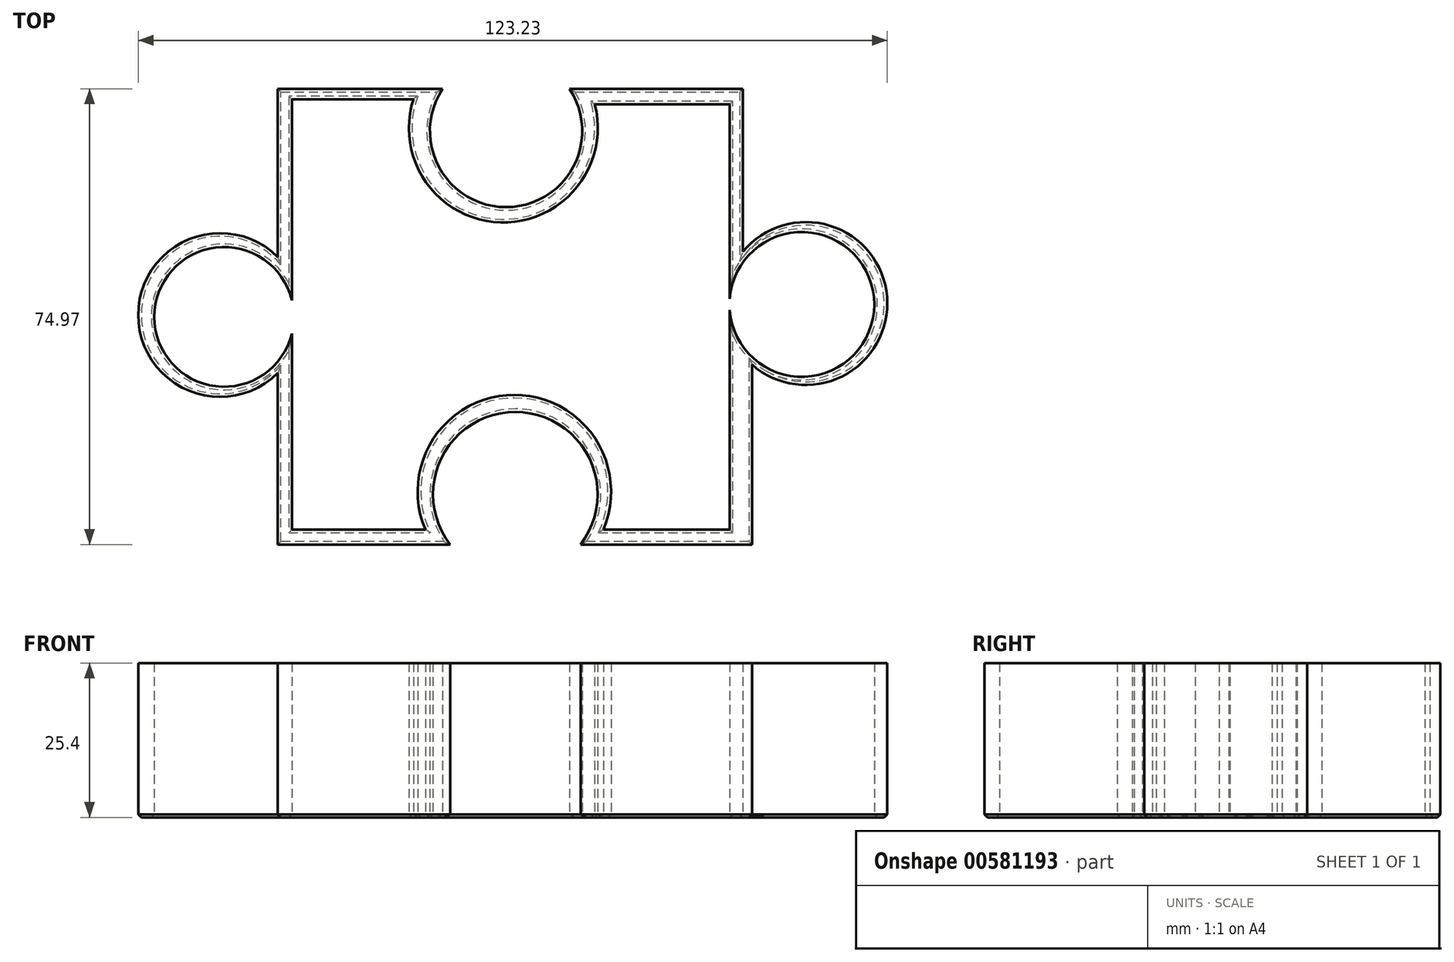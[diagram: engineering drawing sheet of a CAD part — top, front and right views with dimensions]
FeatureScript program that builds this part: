
annotation { "Feature Type Name" : "Feature", "Feature Type Description" : "" }
export const myFeature = defineFeature(function(context is Context, id is Id, definition is map)
    precondition{}
    {
        {
            var Q0;
            Q0=qCreatedBy(makeId("Top.planeOp"),FACE);
            var sketch = newSketch(context, id + "F0", { "sketchPlane" : qUnion([Q0])});
            skLineSegment(sketch, "E0", {"start": v(-36.92, 40.28) * mm, "end": v(-36.92, 12.62) * mm});
            skArc(sketch, "E1", {"start": v(-36.92, 12.62) * mm, "mid": v(-59.9, 3.07) * mm, "end": v(-36.92, -6.47) * mm});
            skLineSegment(sketch, "E2", {"start": v(-36.92, 40.28) * mm, "end": v(-9.81, 40.28) * mm});
            skArc(sketch, "E3", {"start": v(-9.81, 40.28) * mm, "mid": v(0.63, 20.81) * mm, "end": v(11.08, 40.28) * mm});
            skLineSegment(sketch, "E4", {"start": v(11.08, 40.28) * mm, "end": v(39.57, 40.28) * mm});
            skLineSegment(sketch, "E5", {"start": v(39.57, 40.28) * mm, "end": v(39.57, 13.45) * mm});
            skLineSegment(sketch, "E6", {"start": v(-36.92, -6.47) * mm, "end": v(-36.92, -34.7) * mm});
            skLineSegment(sketch, "E7", {"start": v(-36.92, -34.7) * mm, "end": v(-8.57, -34.7) * mm});
            skArc(sketch, "E8", {"start": v(12.88, -34.7) * mm, "mid": v(2.15, -12.88) * mm, "end": v(-8.57, -34.7) * mm});
            skLineSegment(sketch, "E9", {"start": v(12.88, -34.7) * mm, "end": v(41.1, -34.7) * mm});
            skLineSegment(sketch, "E10", {"start": v(41.1, -34.7) * mm, "end": v(41.1, -5.1) * mm});
            skArc(sketch, "E11", {"start": v(41.1, -5.1) * mm, "mid": v(63.3, 6.06) * mm, "end": v(39.57, 13.45) * mm});
            skLineSegment(sketch, "E12", {"start": v(-34.6, -32.22) * mm, "end": v(-12.65, -32.22) * mm});
            skLineSegment(sketch, "E13", {"start": v(-34.6, 38.58) * mm, "end": v(-14.62, 38.58) * mm});
            skPoint(sketch, "E14.end.orphan", {"position": v(-34.6, 12.68) * mm});
            skPoint(sketch, "E15.start.orphan", {"position": v(-34.6, -6.32) * mm});
            skArc(sketch, "E16", {"start": v(-14.62, 38.58) * mm, "mid": v(-0.26, 18.31) * mm, "end": v(15.22, 37.74) * mm});
            skArc(sketch, "E17", {"start": v(16.63, -32.22) * mm, "mid": v(1.99, -10.08) * mm, "end": v(-12.65, -32.22) * mm});
            skLineSegment(sketch, "E18", {"start": v(-34.6, 38.58) * mm, "end": v(-34.6, 12.68) * mm});
            skLineSegment(sketch, "E19", {"start": v(-34.6, -32.22) * mm, "end": v(-34.6, -6.32) * mm});
            skLineSegment(sketch, "E20", {"start": v(-34.6, -6.32) * mm, "end": v(-34.6, 0) * mm});
            skLineSegment(sketch, "E21", {"start": v(-34.6, 12.68) * mm, "end": v(-34.6, 5.5) * mm});
            skArc(sketch, "E22", {"start": v(-34.6, 5.5) * mm, "mid": v(-57.24, 2.75) * mm, "end": v(-34.6, 0) * mm});
            skPoint(sketch, "E23.end.orphan", {"position": v(38.72, 0) * mm});
            skLineSegment(sketch, "E24", {"start": v(16.63, -32.22) * mm, "end": v(37.4, -32.22) * mm});
            skLineSegment(sketch, "E25", {"start": v(37.4, -32.22) * mm, "end": v(37.4, 2.66) * mm});
            skLineSegment(sketch, "E26", {"start": v(37.4, 34.76) * mm, "end": v(37.4, 7.37) * mm});
            skLineSegment(sketch, "E27", {"start": v(15.22, 37.74) * mm, "end": v(37.4, 37.74) * mm});
            skLineSegment(sketch, "E28", {"start": v(37.4, 37.74) * mm, "end": v(37.4, 34.76) * mm});
            skLineSegment(sketch, "E29", {"start": v(37.4, 2.66) * mm, "end": v(37.4, 3.9) * mm});
            skLineSegment(sketch, "E30", {"start": v(37.4, 7.37) * mm, "end": v(37.4, 5.7) * mm});
            skArc(sketch, "E31", {"start": v(37.4, 3.9) * mm, "mid": v(61.2, 4.8) * mm, "end": v(37.4, 5.7) * mm});
            skSolve(sketch);
        }
        {
            var Q0;
            Q0 = qSketchRegion(id + "F0", true);
            extrude(context, id + "F1", {"entities" : qUnion([Q0]), "depth" : 25.4 * mm, "offsetDistance" : 25.4 * mm});
        }
        {
            var Q0;
            Q0=makeQuery(id+"F1.opExtrude","CAP_FACE",FACE,{"disambiguationData":[OSD([sQuery(id+"F0.wireOp",EDGE,"E0"),sQuery(id+"F0.wireOp",EDGE,"E1"),sQuery(id+"F0.wireOp",EDGE,"E2"),sQuery(id+"F0.wireOp",EDGE,"E3"),sQuery(id+"F0.wireOp",EDGE,"E4"),sQuery(id+"F0.wireOp",EDGE,"E5"),sQuery(id+"F0.wireOp",EDGE,"E6"),sQuery(id+"F0.wireOp",EDGE,"E7"),sQuery(id+"F0.wireOp",EDGE,"E8"),sQuery(id+"F0.wireOp",EDGE,"E9"),sQuery(id+"F0.wireOp",EDGE,"E10"),sQuery(id+"F0.wireOp",EDGE,"E11"),sQuery(id+"F0.wireOp",EDGE,"E12"),sQuery(id+"F0.wireOp",EDGE,"E13"),sQuery(id+"F0.wireOp",EDGE,"E16"),sQuery(id+"F0.wireOp",EDGE,"E17"),sQuery(id+"F0.wireOp",EDGE,"E18"),sQuery(id+"F0.wireOp",EDGE,"E19"),sQuery(id+"F0.wireOp",EDGE,"E20"),sQuery(id+"F0.wireOp",EDGE,"E21"),sQuery(id+"F0.wireOp",EDGE,"E22"),sQuery(id+"F0.wireOp",EDGE,"E24"),sQuery(id+"F0.wireOp",EDGE,"E25"),sQuery(id+"F0.wireOp",EDGE,"E26"),sQuery(id+"F0.wireOp",EDGE,"E27"),sQuery(id+"F0.wireOp",EDGE,"E28"),sQuery(id+"F0.wireOp",EDGE,"E29"),sQuery(id+"F0.wireOp",EDGE,"E30"),sQuery(id+"F0.wireOp",EDGE,"E31")])],"isStart":true});
            chamfer(context, id + "F2", {"entities" : qUnion([Q0]), "width" : 0.5 * mm, "tangentPropagation" : true});
        }
    });
